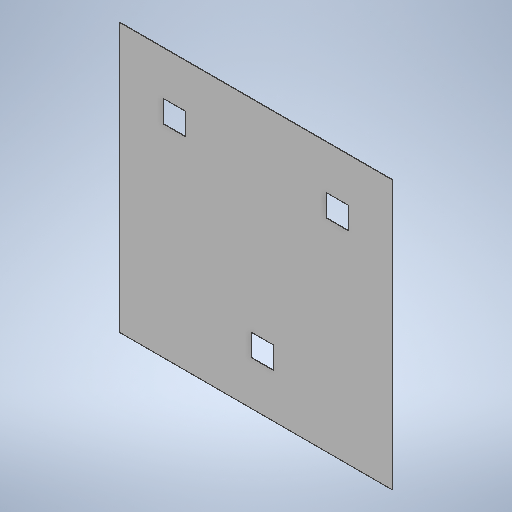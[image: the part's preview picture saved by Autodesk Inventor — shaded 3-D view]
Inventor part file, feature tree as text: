
AUTODESK INVENTOR PART (.ipt)
format: ipt  version: 2025.1 (Build 291241020, 241B)  size: 228,864 bytes
history: native  units: in
note: dims shown in document units (in); Inventor stores cm internally (conversion verified against a paired STEP export)
features: extrude x1, sketch x1
ambient origin geometry x8: Origin, YZ Plane, XZ Plane, XY Plane, X Axis, Y Axis, Z Axis, Center Point
bodies: Solid1 (feature_tree)
feature tree (2):
  extrude  "Extrusion1"  Depth=6.2in
  sketch  "Sketch1"  dims[d0=6.1in d1=6.2in d17=0.01in d18=0.0in d19=0.5in d20=0.5in d21=0.5in d22=0.5in d23=0.5in d24=1.0in d25=1.0in d26=3.0in d27=1.0in d28=1.0in]
